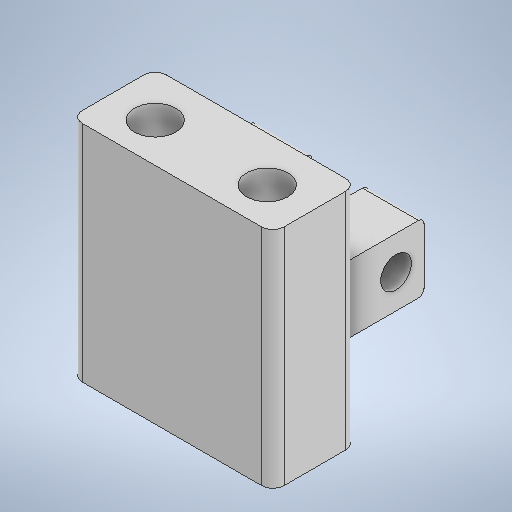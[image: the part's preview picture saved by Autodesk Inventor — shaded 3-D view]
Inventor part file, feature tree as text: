
AUTODESK INVENTOR PART (.ipt)
format: ipt  version: 2025.2 (Build 292293000, 293)  size: 321,024 bytes
history: native  units: mm
features: extrude x6, sketch x6, fillet x4, mirror x3, other x1
ambient origin geometry x8: Origin, YZ Plane, XZ Plane, XY Plane, X Axis, Y Axis, Z Axis, Center Point
bodies: Body1 (feature_tree)
feature tree (20):
  other  "Bryła1"
  extrude  "Wyciągnięcie proste1"  Depth=40.0mm
  sketch  "Szkic3"
  fillet  "Zaokrąglenie1"  Radius=15.0mm
  extrude  "Wyciągnięcie proste3"  Depth=20.0mm TaperAngle=0.0deg
  extrude  "Wyciągnięcie proste4"  Depth=36.0mm
  extrude  "Wyciągnięcie proste6"  Depth=15.0mm
  mirror  "Odbij1"
  extrude  "Wyciągnięcie proste7"  Depth=12.0mm
  mirror  "Odbij3"
  fillet  "Zaokrąglenie4"  Radius=8.0mm
  fillet  "Zaokrąglenie5"  Radius=8.0mm
  fillet  "Zaokrąglenie6"  Radius=12.0mm
  extrude  "Wyciągnięcie proste8"  Depth=8.0mm
  mirror  "Odbij4"
  sketch  "Szkic2"
  sketch  "Szkic4"
  sketch  "Szkic7"
  sketch  "Szkic11"
  sketch  "Szkic12"
